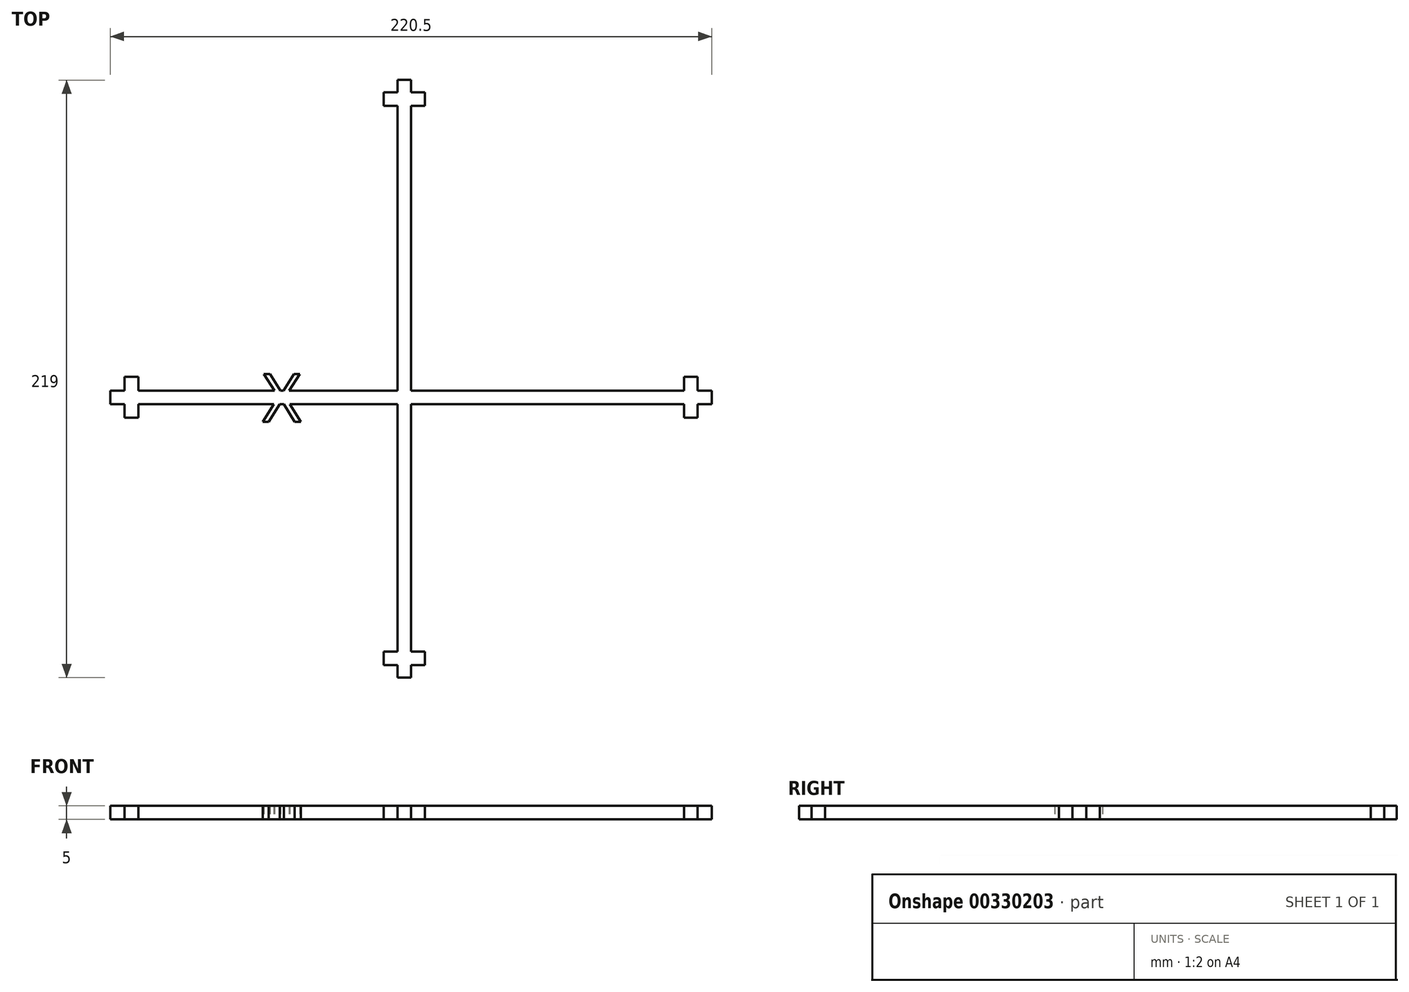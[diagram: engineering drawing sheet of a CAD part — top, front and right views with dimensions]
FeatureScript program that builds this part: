
annotation { "Feature Type Name" : "Feature", "Feature Type Description" : "" }
export const myFeature = defineFeature(function(context is Context, id is Id, definition is map)
    precondition{}
    {
        {
            var Q0;
            Q0=qCreatedBy(makeId("Top.planeOp"),FACE);
            var sketch = newSketch(context, id + "F0", { "sketchPlane" : qUnion([Q0])});
            skLineSegment(sketch, "E0.bottom", {"start": v(-5, 113.81) * mm, "end": v(0, 113.81) * mm});
            skLineSegment(sketch, "E0.top", {"start": v(-5, -105.19) * mm, "end": v(0, -105.19) * mm});
            skLineSegment(sketch, "E0.left", {"start": v(-5, 113.81) * mm, "end": v(-5, -105.19) * mm});
            skLineSegment(sketch, "E0.right", {"start": v(0, 113.81) * mm, "end": v(0, -105.19) * mm});
            skLineSegment(sketch, "E1.bottom", {"start": v(110.25, 0) * mm, "end": v(-110.25, 0) * mm});
            skLineSegment(sketch, "E1.top", {"start": v(110.25, -5) * mm, "end": v(-110.25, -5) * mm});
            skLineSegment(sketch, "E1.left", {"start": v(110.25, 0) * mm, "end": v(110.25, -5) * mm});
            skLineSegment(sketch, "E1.right", {"start": v(-110.25, 0) * mm, "end": v(-110.25, -5) * mm});
            skLineSegment(sketch, "E2.bottom", {"start": v(105, 5) * mm, "end": v(100, 5) * mm});
            skLineSegment(sketch, "E2.top", {"start": v(105, -10) * mm, "end": v(100, -10) * mm});
            skLineSegment(sketch, "E2.left", {"start": v(105, 5) * mm, "end": v(105, -10) * mm});
            skLineSegment(sketch, "E2.right", {"start": v(100, 5) * mm, "end": v(100, -10) * mm});
            skLineSegment(sketch, "E3.bottom", {"start": v(-100, 5) * mm, "end": v(-105, 5) * mm});
            skLineSegment(sketch, "E3.top", {"start": v(-100, -10) * mm, "end": v(-105, -10) * mm});
            skLineSegment(sketch, "E3.left", {"start": v(-100, 5) * mm, "end": v(-100, -10) * mm});
            skLineSegment(sketch, "E3.right", {"start": v(-105, 5) * mm, "end": v(-105, -10) * mm});
            skLineSegment(sketch, "E4.bottom", {"start": v(5, 109.31) * mm, "end": v(-10, 109.31) * mm});
            skLineSegment(sketch, "E4.top", {"start": v(5, 104.31) * mm, "end": v(-10, 104.31) * mm});
            skLineSegment(sketch, "E4.left", {"start": v(5, 109.31) * mm, "end": v(5, 104.31) * mm});
            skLineSegment(sketch, "E4.right", {"start": v(-10, 109.31) * mm, "end": v(-10, 104.31) * mm});
            skLineSegment(sketch, "E5.bottom", {"start": v(5, -95.69) * mm, "end": v(-10, -95.69) * mm});
            skLineSegment(sketch, "E5.top", {"start": v(5, -100.69) * mm, "end": v(-10, -100.69) * mm});
            skLineSegment(sketch, "E5.left", {"start": v(5, -95.69) * mm, "end": v(5, -100.69) * mm});
            skLineSegment(sketch, "E5.right", {"start": v(-10, -95.69) * mm, "end": v(-10, -100.69) * mm});
            skText(sketch, "E6", { "text": "X", "fontName": "OpenSans-Regular.ttf"});
            const initialGuessF0  = {"E6": [-0.05446, -0.01145, 1, 0, 0.01768]};
            skSetInitialGuess(sketch, initialGuessF0);
            skSolve(sketch);
        }
        {
            var Q0;
            {var subQ0=sQuery(id+"F0.wireOp",EDGE,"E1.bottom");var subQ1=sQuery(id+"F0.wireOp",EDGE,"E0.right");var subQ2=makeQuery(id+"F0.imprint","INTERSECT",VERTEX,{"derivedFrom":[subQ1,subQ0]});Q0=makeQuery(id+"F0.imprint","IMPRINT",FACE,{"disambiguationData":[TD([[makeQuery(id+"F0.imprint","IMPRINT",EDGE,{"disambiguationData":[TD([[subQ2,-1.0]])],"derivedFrom":subQ1}),1.0]])]});}
            var Q1;
            {var subQ0=sQuery(id+"F0.wireOp",EDGE,"E2.left");var subQ1=sQuery(id+"F0.wireOp",EDGE,"E1.bottom");var subQ2=makeQuery(id+"F0.imprint","INTERSECT",VERTEX,{"derivedFrom":[subQ1,subQ0]});Q1=makeQuery(id+"F0.imprint","IMPRINT",FACE,{"disambiguationData":[TD([[makeQuery(id+"F0.imprint","IMPRINT",EDGE,{"disambiguationData":[TD([[subQ2,-1.0]])],"derivedFrom":subQ1}),1.0]])]});}
            var Q2;
            {var subQ5=sQuery(id+"F0.wireOp",EDGE,"E2.bottom");Q2=makeQuery(id+"F0.imprint","IMPRINT",FACE,{"disambiguationData":[TD([[makeQuery(id+"F0.imprint","IMPRINT",EDGE,{"derivedFrom":subQ5}),1.0]])]});}
            var Q3;
            {var subQ5=sQuery(id+"F0.wireOp",EDGE,"E2.top");Q3=makeQuery(id+"F0.imprint","IMPRINT",FACE,{"disambiguationData":[TD([[makeQuery(id+"F0.imprint","IMPRINT",EDGE,{"derivedFrom":subQ5}),-1.0]])]});}
            var Q4;
            {var subQ0=sQuery(id+"F0.wireOp",EDGE,"E1.left");Q4=makeQuery(id+"F0.imprint","IMPRINT",FACE,{"disambiguationData":[TD([[makeQuery(id+"F0.imprint","IMPRINT",EDGE,{"derivedFrom":subQ0}),-1.0]])]});}
            var Q5;
            {var subQ3=sQuery(id+"F0.wireOp",EDGE,"E1.bottom");var subQ6=sQuery(id+"F0.wireOp",EDGE,"E0.left");var subQ9=makeQuery(id+"F0.imprint","INTERSECT",VERTEX,{"derivedFrom":[subQ6,subQ3]});Q5=makeQuery(id+"F0.imprint","IMPRINT",FACE,{"disambiguationData":[TD([[makeQuery(id+"F0.imprint","IMPRINT",EDGE,{"disambiguationData":[TD([[subQ9,-1.0]])],"derivedFrom":subQ6}),-1.0]])]});}
            var Q6;
            Q6 = qSketchRegion(id + "F0", true);
            extrude(context, id + "F1", {"entities" : qUnion([Q0, Q1, Q2, Q3, Q4, Q5, Q6]), "depth" : 5 * mm});
        }
    });
